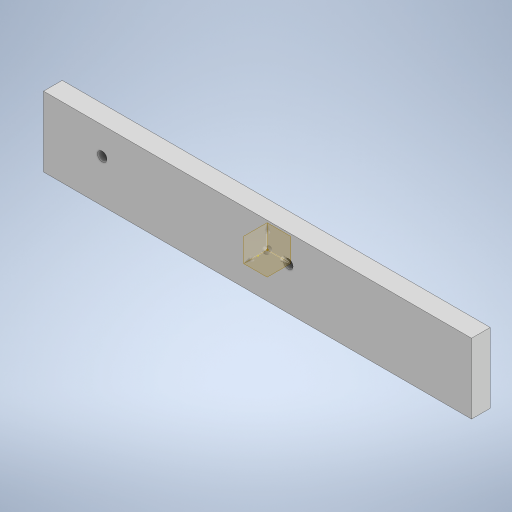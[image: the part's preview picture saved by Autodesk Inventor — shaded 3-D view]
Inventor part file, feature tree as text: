
AUTODESK INVENTOR PART (.ipt)
format: ipt  version: 2024 (Build 280153000, 153)  size: 228,864 bytes
history: native  units: mm
features: other x6, sketch x1
ambient origin geometry x8: Origin, YZ Plane, XZ Plane, XY Plane, X Axis, Y Axis, Z Axis, Center Point
bodies: Body1 (feature_tree)
feature tree (7):
  other  "BORDE_1"
  other  "Generador_de_Piezas.ipt"
  other  "Desplazar cuerpo1"
  other  "Desplazar cuerpo2"
  sketch  "Boceto2"  dims[d0=10.0mm d1=-181.306mm d2=-2388.044mm d3=0.0mm d6=-0.183mm d7=0.023mm d8=0.0mm]
  other  "BORDE_1::Generador_de_Piezas.ipt"
  other  "OperaciónIdentificador1"
